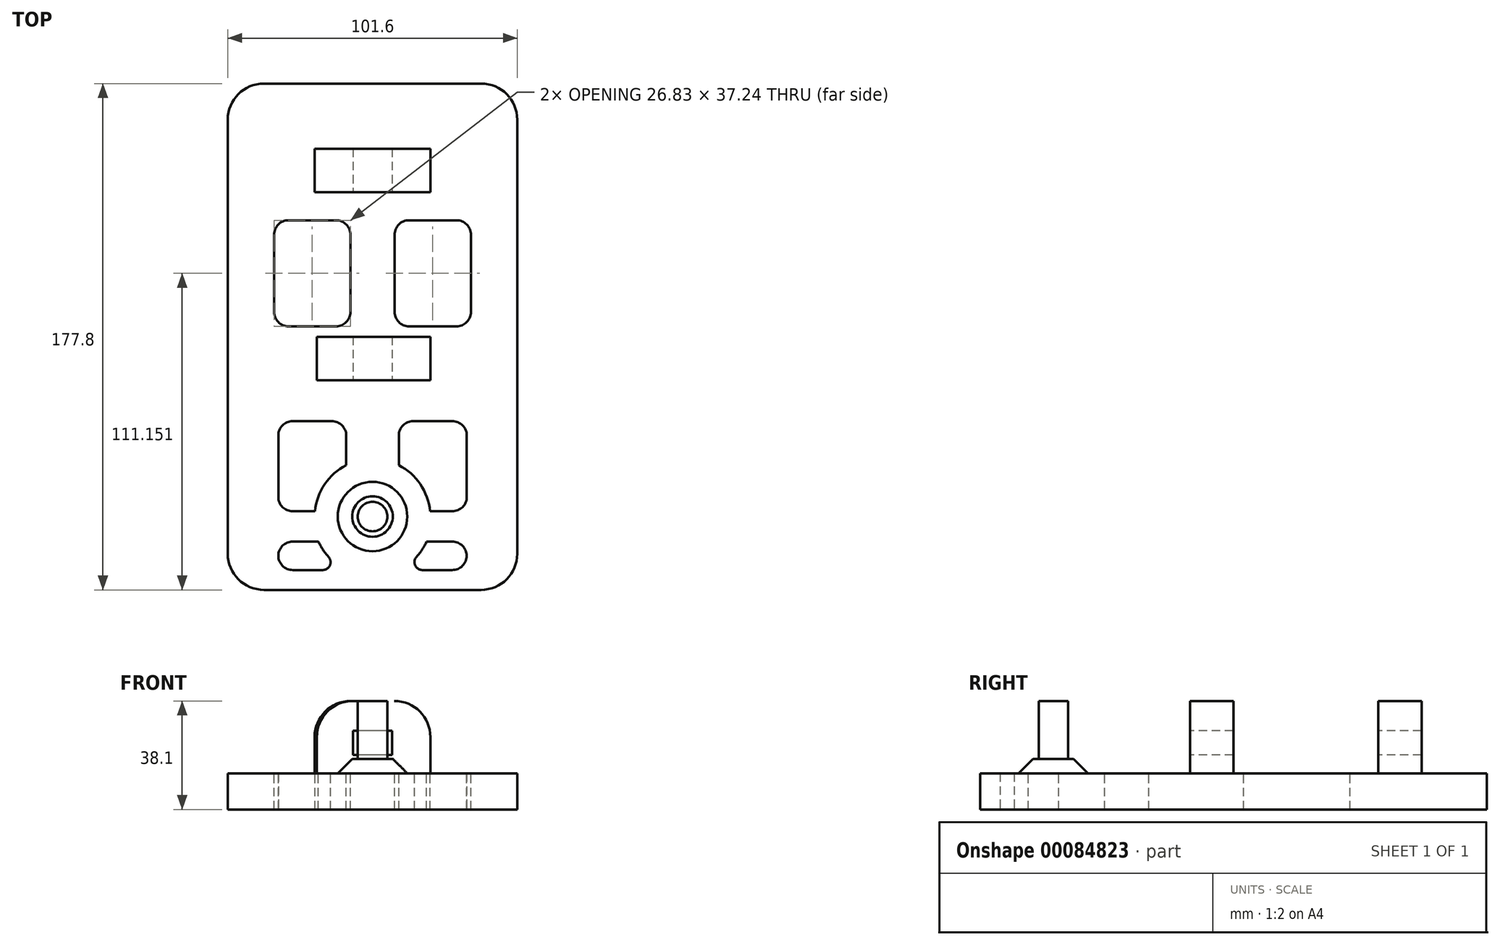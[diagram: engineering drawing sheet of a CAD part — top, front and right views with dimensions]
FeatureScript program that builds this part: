
annotation { "Feature Type Name" : "Feature", "Feature Type Description" : "" }
export const myFeature = defineFeature(function(context is Context, id is Id, definition is map)
    precondition{}
    {
        {
            var Q0;
            Q0=qCreatedBy(makeId("Top.planeOp"),FACE);
            var sketch = newSketch(context, id + "F0", { "sketchPlane" : qUnion([Q0])});
            skLineSegment(sketch, "E0", {"start": v(-50.8, 0) * mm, "end": v(-50.8, 88.9) * mm});
            skLineSegment(sketch, "E1", {"start": v(-50.8, 88.9) * mm, "end": v(0, 88.9) * mm});
            skLineSegment(sketch, "E2.MirrorCS", {"start": v(50.8, 88.9) * mm, "end": v(0, 88.9) * mm});
            skLineSegment(sketch, "E3.MirrorCS", {"start": v(50.8, 0) * mm, "end": v(50.8, 88.9) * mm});
            skLineSegment(sketch, "E4.MirrorCS", {"start": v(-50.8, 0) * mm, "end": v(-50.8, -88.9) * mm});
            skLineSegment(sketch, "E5.MirrorCS", {"start": v(-50.8, -88.9) * mm, "end": v(0, -88.9) * mm});
            skLineSegment(sketch, "E6.MirrorCS", {"start": v(50.8, -88.9) * mm, "end": v(0, -88.9) * mm});
            skLineSegment(sketch, "E7.MirrorCS", {"start": v(50.8, 0) * mm, "end": v(50.8, -88.9) * mm});
            skSolve(sketch);
        }
        {
            var Q0;
            Q0 = qSketchRegion(id + "F0", true);
            extrude(context, id + "F1", {"entities" : qUnion([Q0]), "depth" : 12.7 * mm});
        }
        {
            var Q0;
            Q0=makeQuery(id+"F1.opExtrude","CAP_FACE",FACE,{"disambiguationData":[OSD([sQuery(id+"F0.wireOp",EDGE,"E0"),sQuery(id+"F0.wireOp",EDGE,"E1"),sQuery(id+"F0.wireOp",EDGE,"E2.MirrorCS"),sQuery(id+"F0.wireOp",EDGE,"E3.MirrorCS"),sQuery(id+"F0.wireOp",EDGE,"E4.MirrorCS"),sQuery(id+"F0.wireOp",EDGE,"E5.MirrorCS"),sQuery(id+"F0.wireOp",EDGE,"E6.MirrorCS"),sQuery(id+"F0.wireOp",EDGE,"E7.MirrorCS")])],"isStart":false});
            var sketch = newSketch(context, id + "F2", { "sketchPlane" : qUnion([Q0])});
            skLineSegment(sketch, "E8", {"start": v(0, 66.04) * mm, "end": v(-20.32, 66.04) * mm});
            skLineSegment(sketch, "E9", {"start": v(-20.32, 66.04) * mm, "end": v(-20.32, 50.8) * mm});
            skLineSegment(sketch, "E10", {"start": v(-20.32, 50.8) * mm, "end": v(0, 50.8) * mm});
            skLineSegment(sketch, "E11.MirrorCS", {"start": v(20.32, 50.8) * mm, "end": v(0, 50.8) * mm});
            skLineSegment(sketch, "E12.MirrorCS", {"start": v(20.32, 66.04) * mm, "end": v(20.32, 50.8) * mm});
            skLineSegment(sketch, "E13.MirrorCS", {"start": v(0, 66.04) * mm, "end": v(20.32, 66.04) * mm});
            skLineSegment(sketch, "E14", {"start": v(-19.55, 0) * mm, "end": v(-19.55, -15.24) * mm});
            skLineSegment(sketch, "E15", {"start": v(-19.55, -15.24) * mm, "end": v(0, -15.24) * mm});
            skLineSegment(sketch, "E16", {"start": v(0, -15.24) * mm, "end": v(20.32, -15.24) * mm});
            skLineSegment(sketch, "E17", {"start": v(20.32, -15.24) * mm, "end": v(20.32, 0) * mm});
            skLineSegment(sketch, "E18", {"start": v(0, 0) * mm, "end": v(20.32, 0) * mm});
            skLineSegment(sketch, "E19", {"start": v(-19.55, 0) * mm, "end": v(0, 0) * mm});
            skSolve(sketch);
        }
        {
            var Q0;
            Q0 = qSketchRegion(id + "F2", true);
            extrude(context, id + "F3", {"entities" : qUnion([Q0]), "operationType" : NewBodyOperationType.ADD, "depth" : 25.4 * mm});
        }
        {
            var Q0;
            Q0=makeQuery(id+"F3.opExtrude","CAP_EDGE",EDGE,{"disambiguationData":[OSD([sQuery(id+"F2.wireOp",EDGE,"E17")])],"isStart":false});
            var Q1;
            Q1=makeQuery(id+"F3.opExtrude","CAP_EDGE",EDGE,{"disambiguationData":[OSD([sQuery(id+"F2.wireOp",EDGE,"E14")])],"isStart":false});
            fillet(context, id + "F4", {"entities" : qUnion([Q0, Q1]), "radius" : 12.7 * mm, "tangentPropagation" : true, "allowEdgeOverflow" : false});
        }
        {
            var Q0;
            Q0=makeQuery(id+"F3.opExtrude","CAP_EDGE",EDGE,{"disambiguationData":[OSD([sQuery(id+"F2.wireOp",EDGE,"E12.MirrorCS")])],"isStart":false});
            var Q1;
            Q1=makeQuery(id+"F3.opExtrude","CAP_EDGE",EDGE,{"disambiguationData":[OSD([sQuery(id+"F2.wireOp",EDGE,"E9")])],"isStart":false});
            fillet(context, id + "F5", {"entities" : qUnion([Q0, Q1]), "radius" : 12.7 * mm, "tangentPropagation" : true, "allowEdgeOverflow" : false});
        }
        {
            var Q0;
            Q0=makeQuery(id+"F1.opExtrude","SWEPT_EDGE",EDGE,{"disambiguationData":[OSD([sQuery(id+"F0.wireOp",EDGE,"E2.MirrorCS"),sQuery(id+"F0.wireOp",EDGE,"E3.MirrorCS")])]});
            var Q1;
            Q1=makeQuery(id+"F1.opExtrude","SWEPT_EDGE",EDGE,{"disambiguationData":[OSD([sQuery(id+"F0.wireOp",EDGE,"E0"),sQuery(id+"F0.wireOp",EDGE,"E1")])]});
            var Q2;
            Q2=makeQuery(id+"F1.opExtrude","SWEPT_EDGE",EDGE,{"disambiguationData":[OSD([sQuery(id+"F0.wireOp",EDGE,"E6.MirrorCS"),sQuery(id+"F0.wireOp",EDGE,"E7.MirrorCS")])]});
            var Q3;
            Q3=makeQuery(id+"F1.opExtrude","SWEPT_EDGE",EDGE,{"disambiguationData":[OSD([sQuery(id+"F0.wireOp",EDGE,"E4.MirrorCS"),sQuery(id+"F0.wireOp",EDGE,"E5.MirrorCS")])]});
            fillet(context, id + "F6", {"entities" : qUnion([Q0, Q1, Q2, Q3]), "radius" : 12.7 * mm, "tangentPropagation" : true, "allowEdgeOverflow" : false});
        }
        {
            var Q0;
            Q0=makeQuery(id+"F3.opExtrude","SWEPT_FACE",FACE,{"disambiguationData":[OSD([sQuery(id+"F2.wireOp",EDGE,"E15"),sQuery(id+"F2.wireOp",EDGE,"E16")])]});
            var sketch = newSketch(context, id + "F7", { "sketchPlane" : qUnion([Q0])});
            skLineSegment(sketch, "E20", {"start": v(0, 27.62) * mm, "end": v(-6.85, 27.62) * mm});
            skLineSegment(sketch, "E21", {"start": v(-6.85, 27.62) * mm, "end": v(-6.85, 19.1) * mm});
            skLineSegment(sketch, "E22", {"start": v(-6.85, 19.1) * mm, "end": v(0, 19.1) * mm});
            skLineSegment(sketch, "E23.MirrorCS", {"start": v(0, 27.62) * mm, "end": v(6.85, 27.62) * mm});
            skLineSegment(sketch, "E24.MirrorCS", {"start": v(6.85, 27.62) * mm, "end": v(6.85, 19.1) * mm});
            skLineSegment(sketch, "E25.MirrorCS", {"start": v(6.85, 19.1) * mm, "end": v(0, 19.1) * mm});
            skSolve(sketch);
        }
        {
            var Q0;
            Q0 = qSketchRegion(id + "F7", true);
            extrude(context, id + "F8", {"entities" : qUnion([Q0]), "operationType" : NewBodyOperationType.REMOVE, "endBound" : BoundingType.THROUGH_ALL, "oppositeDirection" : true, "depth" : 25.4 * mm});
        }
        {
            var Q0;
            Q0=makeQuery(id+"F1.opExtrude","CAP_FACE",FACE,{"disambiguationData":[OSD([sQuery(id+"F0.wireOp",EDGE,"E0"),sQuery(id+"F0.wireOp",EDGE,"E1"),sQuery(id+"F0.wireOp",EDGE,"E2.MirrorCS"),sQuery(id+"F0.wireOp",EDGE,"E3.MirrorCS"),sQuery(id+"F0.wireOp",EDGE,"E4.MirrorCS"),sQuery(id+"F0.wireOp",EDGE,"E5.MirrorCS"),sQuery(id+"F0.wireOp",EDGE,"E6.MirrorCS"),sQuery(id+"F0.wireOp",EDGE,"E7.MirrorCS")])],"isStart":false});
            var sketch = newSketch(context, id + "F9", { "sketchPlane" : qUnion([Q0])});
            skLineSegment(sketch, "E26.bottom", {"start": v(-34.56, 40.87) * mm, "end": v(-7.73, 40.87) * mm});
            skLineSegment(sketch, "E26.top", {"start": v(-34.56, 3.63) * mm, "end": v(-7.73, 3.63) * mm});
            skLineSegment(sketch, "E26.left", {"start": v(-34.56, 40.87) * mm, "end": v(-34.56, 3.63) * mm});
            skLineSegment(sketch, "E26.right", {"start": v(-7.73, 40.87) * mm, "end": v(-7.73, 3.63) * mm});
            skLineSegment(sketch, "E27.MirrorCS", {"start": v(7.73, 40.87) * mm, "end": v(7.73, 3.63) * mm});
            skLineSegment(sketch, "E28.MirrorCS", {"start": v(34.56, 40.87) * mm, "end": v(7.73, 40.87) * mm});
            skLineSegment(sketch, "E29.MirrorCS", {"start": v(34.56, 40.87) * mm, "end": v(34.56, 3.63) * mm});
            skLineSegment(sketch, "E30.MirrorCS", {"start": v(34.56, 3.63) * mm, "end": v(7.73, 3.63) * mm});
            skSolve(sketch);
        }
        {
            var Q0;
            Q0 = qSketchRegion(id + "F9", true);
            extrude(context, id + "F10", {"entities" : qUnion([Q0]), "operationType" : NewBodyOperationType.REMOVE, "endBound" : BoundingType.THROUGH_ALL, "oppositeDirection" : true, "depth" : 25.4 * mm});
        }
        {
            var Q0;
            Q0=makeQuery(id+"F10.boolean.opBoolean","COPY",EDGE,{"derivedFrom":makeQuery(id+"F10.opExtrude","SWEPT_EDGE",EDGE,{"disambiguationData":[OSD([sQuery(id+"F9.wireOp",EDGE,"E26.bottom"),sQuery(id+"F9.wireOp",EDGE,"E26.left")])]})});
            var Q1;
            Q1=makeQuery(id+"F10.boolean.opBoolean","COPY",EDGE,{"derivedFrom":makeQuery(id+"F10.opExtrude","SWEPT_EDGE",EDGE,{"disambiguationData":[OSD([sQuery(id+"F9.wireOp",EDGE,"E26.bottom"),sQuery(id+"F9.wireOp",EDGE,"E26.right")])]})});
            var Q2;
            Q2=makeQuery(id+"F10.boolean.opBoolean","COPY",EDGE,{"derivedFrom":makeQuery(id+"F10.opExtrude","SWEPT_EDGE",EDGE,{"disambiguationData":[OSD([sQuery(id+"F9.wireOp",EDGE,"E26.top"),sQuery(id+"F9.wireOp",EDGE,"E26.right")])]})});
            var Q3;
            Q3=makeQuery(id+"F10.boolean.opBoolean","COPY",EDGE,{"derivedFrom":makeQuery(id+"F10.opExtrude","SWEPT_EDGE",EDGE,{"disambiguationData":[OSD([sQuery(id+"F9.wireOp",EDGE,"E26.top"),sQuery(id+"F9.wireOp",EDGE,"E26.left")])]})});
            var Q4;
            Q4=makeQuery(id+"F10.boolean.opBoolean","COPY",EDGE,{"derivedFrom":makeQuery(id+"F10.opExtrude","SWEPT_EDGE",EDGE,{"disambiguationData":[OSD([sQuery(id+"F9.wireOp",EDGE,"E29.MirrorCS"),sQuery(id+"F9.wireOp",EDGE,"E30.MirrorCS")])]})});
            var Q5;
            Q5=makeQuery(id+"F10.boolean.opBoolean","COPY",EDGE,{"derivedFrom":makeQuery(id+"F10.opExtrude","SWEPT_EDGE",EDGE,{"disambiguationData":[OSD([sQuery(id+"F9.wireOp",EDGE,"E27.MirrorCS"),sQuery(id+"F9.wireOp",EDGE,"E30.MirrorCS")])]})});
            var Q6;
            Q6=makeQuery(id+"F10.boolean.opBoolean","COPY",EDGE,{"derivedFrom":makeQuery(id+"F10.opExtrude","SWEPT_EDGE",EDGE,{"disambiguationData":[OSD([sQuery(id+"F9.wireOp",EDGE,"E27.MirrorCS"),sQuery(id+"F9.wireOp",EDGE,"E28.MirrorCS")])]})});
            var Q7;
            Q7=makeQuery(id+"F10.boolean.opBoolean","COPY",EDGE,{"derivedFrom":makeQuery(id+"F10.opExtrude","SWEPT_EDGE",EDGE,{"disambiguationData":[OSD([sQuery(id+"F9.wireOp",EDGE,"E28.MirrorCS"),sQuery(id+"F9.wireOp",EDGE,"E29.MirrorCS")])]})});
            var Q8;
            Q8=makeQuery(id+"F10.boolean.opBoolean","COPY",EDGE,{"derivedFrom":makeQuery(id+"F10.opExtrude","SWEPT_EDGE",EDGE,{"disambiguationData":[OSD([sQuery(id+"F9.wireOp",EDGE,"acf83a67-275e-4b6b-8d6a-00bc1d506a3c0.MirrorCS"),sQuery(id+"F9.wireOp",EDGE,"f95079e9-c2e2-41a1-8624-471fc7e21db50.MirrorCS")])]})});
            var Q9;
            Q9=makeQuery(id+"F10.boolean.opBoolean","COPY",EDGE,{"derivedFrom":makeQuery(id+"F10.opExtrude","SWEPT_EDGE",EDGE,{"disambiguationData":[OSD([sQuery(id+"F9.wireOp",EDGE,"52e567ef-07f4-4b2b-89c8-a6eac041be480.MirrorCS"),sQuery(id+"F9.wireOp",EDGE,"acf83a67-275e-4b6b-8d6a-00bc1d506a3c0.MirrorCS")])]})});
            var Q10;
            Q10=makeQuery(id+"F10.boolean.opBoolean","COPY",EDGE,{"derivedFrom":makeQuery(id+"F10.opExtrude","SWEPT_EDGE",EDGE,{"disambiguationData":[OSD([sQuery(id+"F9.wireOp",EDGE,"52e567ef-07f4-4b2b-89c8-a6eac041be480.MirrorCS"),sQuery(id+"F9.wireOp",EDGE,"9209a13e-bdf6-4ffb-b9ec-bd52a3e9f9210.MirrorCS")])]})});
            var Q11;
            Q11=makeQuery(id+"F10.boolean.opBoolean","COPY",EDGE,{"derivedFrom":makeQuery(id+"F10.opExtrude","SWEPT_EDGE",EDGE,{"disambiguationData":[OSD([sQuery(id+"F9.wireOp",EDGE,"9209a13e-bdf6-4ffb-b9ec-bd52a3e9f9210.MirrorCS"),sQuery(id+"F9.wireOp",EDGE,"f95079e9-c2e2-41a1-8624-471fc7e21db50.MirrorCS")])]})});
            var Q12;
            Q12=makeQuery(id+"F10.boolean.opBoolean","COPY",EDGE,{"derivedFrom":makeQuery(id+"F10.opExtrude","SWEPT_EDGE",EDGE,{"disambiguationData":[OSD([sQuery(id+"F9.wireOp",EDGE,"6J8G5m5A-hJhQ-lYpK-XNNN-3X6anQOs88sd.top"),sQuery(id+"F9.wireOp",EDGE,"6J8G5m5A-hJhQ-lYpK-XNNN-3X6anQOs88sd.left")])]})});
            var Q13;
            Q13=makeQuery(id+"F10.boolean.opBoolean","COPY",EDGE,{"derivedFrom":makeQuery(id+"F10.opExtrude","SWEPT_EDGE",EDGE,{"disambiguationData":[OSD([sQuery(id+"F9.wireOp",EDGE,"6J8G5m5A-hJhQ-lYpK-XNNN-3X6anQOs88sd.bottom"),sQuery(id+"F9.wireOp",EDGE,"6J8G5m5A-hJhQ-lYpK-XNNN-3X6anQOs88sd.left")])]})});
            var Q14;
            Q14=makeQuery(id+"F10.boolean.opBoolean","COPY",EDGE,{"derivedFrom":makeQuery(id+"F10.opExtrude","SWEPT_EDGE",EDGE,{"disambiguationData":[OSD([sQuery(id+"F9.wireOp",EDGE,"6J8G5m5A-hJhQ-lYpK-XNNN-3X6anQOs88sd.bottom"),sQuery(id+"F9.wireOp",EDGE,"6J8G5m5A-hJhQ-lYpK-XNNN-3X6anQOs88sd.right")])]})});
            var Q15;
            Q15=makeQuery(id+"F10.boolean.opBoolean","COPY",EDGE,{"derivedFrom":makeQuery(id+"F10.opExtrude","SWEPT_EDGE",EDGE,{"disambiguationData":[OSD([sQuery(id+"F9.wireOp",EDGE,"6J8G5m5A-hJhQ-lYpK-XNNN-3X6anQOs88sd.top"),sQuery(id+"F9.wireOp",EDGE,"6J8G5m5A-hJhQ-lYpK-XNNN-3X6anQOs88sd.right")])]})});
            fillet(context, id + "F11", {"entities" : qUnion([Q0, Q1, Q2, Q3, Q4, Q5, Q6, Q7, Q8, Q9, Q10, Q11, Q12, Q13, Q14, Q15]), "radius" : 5.08 * mm, "tangentPropagation" : true, "allowEdgeOverflow" : false});
        }
        {
            var Q0;
            Q0=makeQuery(id+"F1.opExtrude","CAP_FACE",FACE,{"disambiguationData":[OSD([sQuery(id+"F0.wireOp",EDGE,"E0"),sQuery(id+"F0.wireOp",EDGE,"E1"),sQuery(id+"F0.wireOp",EDGE,"E2.MirrorCS"),sQuery(id+"F0.wireOp",EDGE,"E3.MirrorCS"),sQuery(id+"F0.wireOp",EDGE,"E4.MirrorCS"),sQuery(id+"F0.wireOp",EDGE,"E5.MirrorCS"),sQuery(id+"F0.wireOp",EDGE,"E6.MirrorCS"),sQuery(id+"F0.wireOp",EDGE,"E7.MirrorCS")])],"isStart":false});
            var sketch = newSketch(context, id + "F12", { "sketchPlane" : qUnion([Q0])});
            skCircle(sketch, "E31", {"center": v(0, -63.15) * mm, "radius": 12.2 * mm});
            skCircle(sketch, "E32", {"center": v(0, -63.15) * mm, "radius": 5.18 * mm});
            skSolve(sketch);
        }
        {
            var Q0;
            Q0=makeQuery(id+"F12.imprint","IMPRINT",FACE,{"disambiguationData":[TD([[makeQuery(id+"F12.imprint","IMPRINT",EDGE,{"derivedFrom":sQuery(id+"F12.wireOp",EDGE,"E31")}),1.0]])]});
            var Q1;
            Q1=sQuery(id+"F12.wireOp",EDGE,"E31");
            extrude(context, id + "F13", {"entities" : qUnion([Q0]), "operationType" : NewBodyOperationType.ADD, "surfaceEntities" : qUnion([Q1]), "depth" : 5.08 * mm});
        }
        {
            var Q0;
            Q0=makeQuery(id+"F13.boolean.opBoolean","SPLIT",FACE,{"disambiguationData":[TD([makeQuery(id+"F13.opExtrude","SWEPT_FACE",FACE,{"disambiguationData":[OSD([sQuery(id+"F12.wireOp",EDGE,"E32")])]})])],"derivedFrom":makeQuery(id+"F1.opExtrude","CAP_FACE",FACE,{"disambiguationData":[OSD([sQuery(id+"F0.wireOp",EDGE,"E0"),sQuery(id+"F0.wireOp",EDGE,"E1"),sQuery(id+"F0.wireOp",EDGE,"E2.MirrorCS"),sQuery(id+"F0.wireOp",EDGE,"E3.MirrorCS"),sQuery(id+"F0.wireOp",EDGE,"E4.MirrorCS"),sQuery(id+"F0.wireOp",EDGE,"E5.MirrorCS"),sQuery(id+"F0.wireOp",EDGE,"E6.MirrorCS"),sQuery(id+"F0.wireOp",EDGE,"E7.MirrorCS")])],"isStart":false})});
            extrude(context, id + "F14", {"entities" : qUnion([Q0]), "operationType" : NewBodyOperationType.ADD, "depth" : 25.4 * mm});
        }
        {
            var Q0;
            Q0=makeQuery(id+"F13.opExtrude","CAP_EDGE",EDGE,{"disambiguationData":[OSD([sQuery(id+"F12.wireOp",EDGE,"E31")])],"isStart":false});
            chamfer(context, id + "F15", {"entities" : qUnion([Q0]), "width" : 5.08 * mm, "tangentPropagation" : true});
        }
        {
            var Q0;
            {var subQ4=sQuery(id+"F0.wireOp",EDGE,"E7.MirrorCS");var subQ5=sQuery(id+"F0.wireOp",EDGE,"E6.MirrorCS");var subQ6=sQuery(id+"F0.wireOp",EDGE,"E3.MirrorCS");var subQ7=sQuery(id+"F0.wireOp",EDGE,"E2.MirrorCS");var subQ8=sQuery(id+"F0.wireOp",EDGE,"E1");var subQ9=sQuery(id+"F0.wireOp",EDGE,"E0");var subQ14=sQuery(id+"F0.wireOp",EDGE,"E5.MirrorCS");var subQ15=sQuery(id+"F0.wireOp",EDGE,"E4.MirrorCS");Q0=makeQuery(id+"F13.boolean.opBoolean","SPLIT",FACE,{"disambiguationData":[TD([makeQuery(id+"F3.opExtrude","SWEPT_FACE",FACE,{"disambiguationData":[OSD([sQuery(id+"F2.wireOp",EDGE,"E9")])]})])],"derivedFrom":makeQuery(id+"F1.opExtrude","CAP_FACE",FACE,{"disambiguationData":[OSD([subQ9,subQ8,subQ7,subQ6,subQ15,subQ14,subQ5,subQ4])],"isStart":false})});}
            var sketch = newSketch(context, id + "F16", { "sketchPlane" : qUnion([Q0])});
            skLineSegment(sketch, "E33", {"start": v(-33.07, -29.64) * mm, "end": v(-9.22, -29.64) * mm});
            skPoint(sketch, "E33.startSnap0", {"position": v(-33.07, 5.12) * mm});
            skPoint(sketch, "E33.endSnap0", {"position": v(-9.22, 5.12) * mm});
            skLineSegment(sketch, "E34", {"start": v(-9.22, -29.64) * mm, "end": v(-9.22, -45.1) * mm});
            skLineSegment(sketch, "E35.MirrorCS", {"start": v(9.22, -29.64) * mm, "end": v(9.22, -45.1) * mm});
            skLineSegment(sketch, "E36.MirrorCS", {"start": v(33.07, -29.64) * mm, "end": v(9.22, -29.64) * mm});
            skArc(sketch, "E37", {"start": v(-9.22, -45.1) * mm, "mid": v(-16.78, -51.8) * mm, "end": v(-20.18, -61.3) * mm});
            skArc(sketch, "E38.MirrorCS", {"start": v(9.22, -45.1) * mm, "mid": v(16.78, -51.8) * mm, "end": v(20.18, -61.3) * mm});
            skLineSegment(sketch, "E39", {"start": v(-20.18, -61.3) * mm, "end": v(-33.07, -61.3) * mm});
            skLineSegment(sketch, "E40", {"start": v(-33.07, -61.3) * mm, "end": v(-33.07, -29.64) * mm});
            skLineSegment(sketch, "E41", {"start": v(20.18, -61.3) * mm, "end": v(33.07, -61.3) * mm});
            skLineSegment(sketch, "E42", {"start": v(33.07, -61.3) * mm, "end": v(33.07, -29.64) * mm});
            skSolve(sketch);
        }
        {
            var Q0;
            Q0 = qSketchRegion(id + "F16", true);
            extrude(context, id + "F17", {"entities" : qUnion([Q0]), "operationType" : NewBodyOperationType.REMOVE, "oppositeDirection" : true, "depth" : 25.4 * mm});
        }
        {
            var Q0;
            Q0=makeQuery(id+"F17.boolean.opBoolean","COPY",EDGE,{"derivedFrom":makeQuery(id+"F17.opExtrude","SWEPT_EDGE",EDGE,{"disambiguationData":[OSD([sQuery(id+"F16.wireOp",EDGE,"E33"),sQuery(id+"F16.wireOp",EDGE,"6LQkuVl8-gjab-eLB5-eliF-n3uNfMPZ1myo")])]})});
            var Q1;
            Q1=makeQuery(id+"F17.boolean.opBoolean","COPY",EDGE,{"derivedFrom":makeQuery(id+"F17.opExtrude","SWEPT_EDGE",EDGE,{"disambiguationData":[OSD([sQuery(id+"F16.wireOp",EDGE,"E36.MirrorCS"),sQuery(id+"F16.wireOp",EDGE,"2ad462b8-a4ba-483e-bd95-7f611b1a8ff30.MirrorCS")])]})});
            var Q2;
            Q2=makeQuery(id+"F17.boolean.opBoolean","COPY",EDGE,{"derivedFrom":makeQuery(id+"F17.opExtrude","SWEPT_EDGE",EDGE,{"disambiguationData":[OSD([sQuery(id+"F16.wireOp",EDGE,"2ad462b8-a4ba-483e-bd95-7f611b1a8ff30.MirrorCS"),sQuery(id+"F16.wireOp",EDGE,"bbe228f5-4316-42cd-8978-1fdf15da6a5a0.MirrorCS")])]})});
            var Q3;
            Q3=makeQuery(id+"F17.boolean.opBoolean","COPY",EDGE,{"derivedFrom":makeQuery(id+"F17.opExtrude","SWEPT_EDGE",EDGE,{"disambiguationData":[OSD([sQuery(id+"F16.wireOp",EDGE,"6LQkuVl8-gjab-eLB5-eliF-n3uNfMPZ1myo"),sQuery(id+"F16.wireOp",EDGE,"1jE0PVti-PXpb-lxS2-TifL-469tvoxKJuie")])]})});
            fillet(context, id + "F18", {"entities" : qUnion([Q0, Q1, Q2, Q3]), "radius" : 5.08 * mm, "tangentPropagation" : true, "allowEdgeOverflow" : false});
        }
        {
            var Q0;
            Q0 = qSketchRegion(id + "F16", true);
            extrude(context, id + "F19", {"entities" : qUnion([Q0]), "operationType" : NewBodyOperationType.REMOVE, "endBound" : BoundingType.THROUGH_ALL, "oppositeDirection" : true, "depth" : 25.4 * mm});
        }
        {
            var Q0;
            {var subQ4=sQuery(id+"F0.wireOp",EDGE,"E7.MirrorCS");var subQ5=sQuery(id+"F0.wireOp",EDGE,"E6.MirrorCS");var subQ6=sQuery(id+"F0.wireOp",EDGE,"E3.MirrorCS");var subQ7=sQuery(id+"F0.wireOp",EDGE,"E2.MirrorCS");var subQ8=sQuery(id+"F0.wireOp",EDGE,"E1");var subQ9=sQuery(id+"F0.wireOp",EDGE,"E0");var subQ14=sQuery(id+"F0.wireOp",EDGE,"E5.MirrorCS");var subQ15=sQuery(id+"F0.wireOp",EDGE,"E4.MirrorCS");Q0=makeQuery(id+"F13.boolean.opBoolean","SPLIT",FACE,{"disambiguationData":[TD([makeQuery(id+"F3.opExtrude","SWEPT_FACE",FACE,{"disambiguationData":[OSD([sQuery(id+"F2.wireOp",EDGE,"E9")])]})])],"derivedFrom":makeQuery(id+"F1.opExtrude","CAP_FACE",FACE,{"disambiguationData":[OSD([subQ9,subQ8,subQ7,subQ6,subQ15,subQ14,subQ5,subQ4])],"isStart":false})});}
            var sketch = newSketch(context, id + "F20", { "sketchPlane" : qUnion([Q0])});
            skArc(sketch, "E43", {"start": v(-9.22, -81.93) * mm, "mid": v(-14.96, -77.78) * mm, "end": v(-18.98, -71.94) * mm});
            skArc(sketch, "E44.MirrorCS", {"start": v(9.22, -81.93) * mm, "mid": v(14.96, -77.78) * mm, "end": v(18.98, -71.94) * mm});
            skLineSegment(sketch, "E45", {"start": v(-18.98, -71.94) * mm, "end": v(-33.07, -71.94) * mm});
            skLineSegment(sketch, "E46", {"start": v(-33.07, -71.94) * mm, "end": v(-33.07, -81.93) * mm});
            skLineSegment(sketch, "E47", {"start": v(-33.07, -81.93) * mm, "end": v(-9.22, -81.93) * mm});
            skLineSegment(sketch, "E48.MirrorCS", {"start": v(33.07, -71.94) * mm, "end": v(33.07, -81.93) * mm});
            skLineSegment(sketch, "E49.MirrorCS", {"start": v(18.98, -71.94) * mm, "end": v(33.07, -71.94) * mm});
            skLineSegment(sketch, "E50.MirrorCS", {"start": v(33.07, -81.93) * mm, "end": v(9.22, -81.93) * mm});
            skSolve(sketch);
        }
        {
            var Q0;
            Q0 = qSketchRegion(id + "F20", true);
            extrude(context, id + "F21", {"entities" : qUnion([Q0]), "operationType" : NewBodyOperationType.REMOVE, "endBound" : BoundingType.THROUGH_ALL, "oppositeDirection" : true, "depth" : 25.4 * mm});
        }
        {
            var Q0;
            Q0=makeQuery(id+"F19.boolean.opBoolean","COPY",EDGE,{"derivedFrom":makeQuery(id+"F19.opExtrude","SWEPT_EDGE",EDGE,{"disambiguationData":[OSD([sQuery(id+"F16.wireOp",EDGE,"E33"),sQuery(id+"F16.wireOp",EDGE,"E34")])]})});
            var Q1;
            Q1=makeQuery(id+"F19.boolean.opBoolean","COPY",EDGE,{"derivedFrom":makeQuery(id+"F19.opExtrude","SWEPT_EDGE",EDGE,{"disambiguationData":[OSD([sQuery(id+"F16.wireOp",EDGE,"E33"),sQuery(id+"F16.wireOp",EDGE,"E40")])]})});
            var Q2;
            Q2=makeQuery(id+"F17.boolean.opBoolean","COPY",EDGE,{"derivedFrom":makeQuery(id+"F17.opExtrude","SWEPT_EDGE",EDGE,{"disambiguationData":[OSD([sQuery(id+"F16.wireOp",EDGE,"E39"),sQuery(id+"F16.wireOp",EDGE,"E40")])]})});
            var Q3;
            Q3=makeQuery(id+"F19.boolean.opBoolean","COPY",EDGE,{"derivedFrom":makeQuery(id+"F19.opExtrude","SWEPT_EDGE",EDGE,{"disambiguationData":[OSD([sQuery(id+"F16.wireOp",EDGE,"E36.MirrorCS"),sQuery(id+"F16.wireOp",EDGE,"E42")])]})});
            var Q4;
            Q4=makeQuery(id+"F19.boolean.opBoolean","COPY",EDGE,{"derivedFrom":makeQuery(id+"F19.opExtrude","SWEPT_EDGE",EDGE,{"disambiguationData":[OSD([sQuery(id+"F16.wireOp",EDGE,"E35.MirrorCS"),sQuery(id+"F16.wireOp",EDGE,"E36.MirrorCS")])]})});
            var Q5;
            Q5=makeQuery(id+"F17.boolean.opBoolean","COPY",EDGE,{"derivedFrom":makeQuery(id+"F17.opExtrude","SWEPT_EDGE",EDGE,{"disambiguationData":[OSD([sQuery(id+"F16.wireOp",EDGE,"E41"),sQuery(id+"F16.wireOp",EDGE,"E42")])]})});
            var Q6;
            Q6=makeQuery(id+"F21.boolean.opBoolean","COPY",EDGE,{"derivedFrom":makeQuery(id+"F21.opExtrude","SWEPT_EDGE",EDGE,{"disambiguationData":[OSD([sQuery(id+"F20.wireOp",EDGE,"E46"),sQuery(id+"F20.wireOp",EDGE,"E47")])]})});
            var Q7;
            Q7=makeQuery(id+"F21.boolean.opBoolean","COPY",EDGE,{"derivedFrom":makeQuery(id+"F21.opExtrude","SWEPT_EDGE",EDGE,{"disambiguationData":[OSD([sQuery(id+"F20.wireOp",EDGE,"E45"),sQuery(id+"F20.wireOp",EDGE,"E46")])]})});
            var Q8;
            Q8=makeQuery(id+"F21.boolean.opBoolean","COPY",EDGE,{"derivedFrom":makeQuery(id+"F21.opExtrude","SWEPT_EDGE",EDGE,{"disambiguationData":[OSD([sQuery(id+"F20.wireOp",EDGE,"E48.MirrorCS"),sQuery(id+"F20.wireOp",EDGE,"E49.MirrorCS")])]})});
            var Q9;
            Q9=makeQuery(id+"F21.boolean.opBoolean","COPY",EDGE,{"derivedFrom":makeQuery(id+"F21.opExtrude","SWEPT_EDGE",EDGE,{"disambiguationData":[OSD([sQuery(id+"F20.wireOp",EDGE,"E48.MirrorCS"),sQuery(id+"F20.wireOp",EDGE,"E50.MirrorCS")])]})});
            fillet(context, id + "F22", {"entities" : qUnion([Q0, Q1, Q2, Q3, Q4, Q5, Q6, Q7, Q8, Q9]), "radius" : 5.08 * mm, "tangentPropagation" : true, "allowEdgeOverflow" : false});
        }
        {
            var Q0;
            Q0=makeQuery(id+"F21.boolean.opBoolean","COPY",EDGE,{"derivedFrom":makeQuery(id+"F21.opExtrude","SWEPT_EDGE",EDGE,{"disambiguationData":[OSD([sQuery(id+"F20.wireOp",EDGE,"E44.MirrorCS"),sQuery(id+"F20.wireOp",EDGE,"E50.MirrorCS")])]})});
            var Q1;
            Q1=makeQuery(id+"F21.boolean.opBoolean","COPY",EDGE,{"derivedFrom":makeQuery(id+"F21.opExtrude","SWEPT_EDGE",EDGE,{"disambiguationData":[OSD([sQuery(id+"F20.wireOp",EDGE,"E43"),sQuery(id+"F20.wireOp",EDGE,"E47")])]})});
            fillet(context, id + "F23", {"entities" : qUnion([Q0, Q1]), "radius" : 2.8 * mm, "tangentPropagation" : true, "allowEdgeOverflow" : false});
        }
    });
